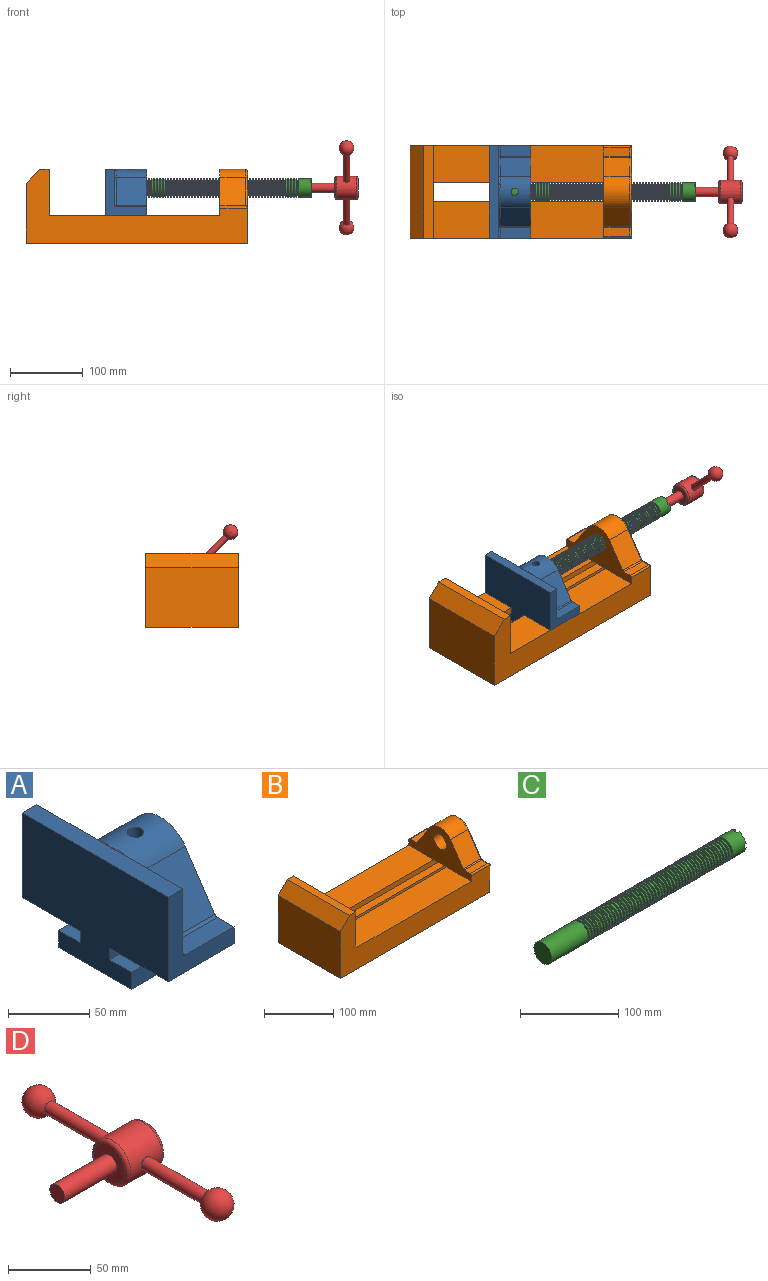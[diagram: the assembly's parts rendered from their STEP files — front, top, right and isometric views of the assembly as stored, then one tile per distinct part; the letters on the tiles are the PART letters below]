
ASSEMBLY  parts=4 mates=3
PART A: 36 faces, bbox 57.2x127x89 mm
  f0: plane 57.15x50.8mm, normal (0,0,-1), area 2903.2mm2, adj f6,f9,f10,f23
  f1: cylinder r=12.7mm len=44.45mm, axis (1,0,0), area 3464.3mm2, adj f6,f15,f16
  f2: plane 41.91x14.52mm, normal (0,0,1), area 608.5mm2, adj f6,f11,f24,f25
  f3: plane 51.86x48.26mm, normal (1,0,0), area 1495.7mm2, adj f8,f10,f31,f33,f35
  f4: plane 51.86x48.26mm, normal (1,0,0), area 1495.7mm2, adj f8,f11,f24,f28,f29
  f5: plane 57.15x50.8mm, normal (0,0,-1), area 2903.2mm2, adj f6,f9,f11,f22
  f6: plane 127x85.09mm, normal (1,0,0), area 5190.6mm2, adj f0,f1,f2,f5,f7,f10,f11,f12
  f7: plane 41.91x14.52mm, normal (0,0,1), area 608.5mm2, adj f6,f10,f30,f31
  f8: plane 127x12.7mm, normal (0,0,1), area 1612.9mm2, adj f3,f4,f9,f10,f11,f26,f34
  f9: plane 127x85.09mm, normal (-1,0,0), area 9096.8mm2, adj f0,f5,f8,f10,f11,f17,f18,f19
  f10: plane 63.5x57.15mm, normal (0,-1,0), area 1372.3mm2, adj f0,f3,f6,f7,f8,f9,f31
  f11: plane 63.5x57.15mm, normal (0,1,0), area 1372.3mm2, adj f2,f4,f5,f6,f8,f9,f24
  f12: plane 41.91x38.43mm, normal (0,-0.83,0.56), area 1939.2mm2, adj f6,f13,f30,f33
  f13: cylinder r=25.4mm len=44.45mm, axis (1,0,0), area 2026.5mm2, adj f6,f12,f14,f16,f26,f28,f34,f35
  f14: plane 41.91x38.43mm, normal (0,0.83,0.56), area 1939.2mm2, adj f6,f13,f25,f29
  f15: plane 25.4x25.4mm, normal (1,0,0), area 506.7mm2, adj f1
  f16: cylinder r=5.08mm len=13.76mm, axis (0,0,1), area 414mm2, adj f1,f13
  f17: plane 57.15x19.05mm, normal (0,0,1), area 1088.7mm2, adj f6,f9,f18,f23
  f18: plane 57.15x12.7mm, normal (0,-1,0), area 725.8mm2, adj f6,f9,f17,f19
  f19: plane 63.5x57.15mm, normal (0,0,-1), area 3629mm2, adj f6,f9,f18,f20
  f20: plane 57.15x12.7mm, normal (0,1,0), area 725.8mm2, adj f6,f9,f19,f21
  f21: plane 57.15x19.05mm, normal (0,0,1), area 1088.7mm2, adj f6,f9,f20,f22
  f22: plane 57.15x8.89mm, normal (0,1,0), area 508.1mm2, adj f5,f6,f9,f21
  f23: plane 57.15x8.89mm, normal (0,-1,0), area 508.1mm2, adj f0,f6,f9,f17
  f24: cylinder r=2.54mm len=14.52mm, axis (0,-1,0), area 57.9mm2, adj f2,f4,f11,f27
  f25: cylinder r=2.54mm len=41.91mm, axis (1,0,0), area 104.3mm2, adj f2,f6,f14,f27
  f26: bspline ~12.24x2.8mm, area 20.9mm2, adj f8,f13,f28
  f27: sphere r=2.54mm, area 6.3mm2, adj f24,f25,f29
  f28: torus R=27.94mm, axis (1,0,0), area 57.8mm2, adj f4,f13,f26,f29
  f29: cylinder r=2.54mm len=39.84mm, axis (0,-0.56,0.83), area 184.6mm2, adj f4,f14,f27,f28
  f30: cylinder r=2.54mm len=41.91mm, axis (1,0,0), area 104.3mm2, adj f6,f7,f12,f32
  f31: cylinder r=2.54mm len=14.52mm, axis (0,-1,0), area 57.9mm2, adj f3,f7,f10,f32
  f32: sphere r=2.54mm, area 6.3mm2, adj f30,f31,f33
  f33: cylinder r=2.54mm len=39.84mm, axis (0,-0.56,-0.83), area 184.6mm2, adj f3,f12,f32,f35
  f34: bspline ~12.24x2.8mm, area 20.9mm2, adj f8,f13,f35
  f35: torus R=27.94mm, axis (1,0,0), area 57.8mm2, adj f3,f13,f33,f34
PART B: 39 faces, bbox 304.8x127x103.7 mm
  f0: plane 234.95x50.8mm, normal (0,0,1), area 11935.5mm2, adj f3,f8,f16,f26
  f1: plane 127x99.06mm, normal (1,0,0), area 7097.5mm2, adj f7,f8,f9,f14,f17,f18,f19,f20
  f2: plane 234.95x50.8mm, normal (0,0,1), area 11935.5mm2, adj f3,f9,f16,f27
  f3: plane 127x101.6mm, normal (1,0,0), area 9516.1mm2, adj f0,f2,f4,f7,f8,f9,f18,f19
  f4: plane 127x12.7mm, normal (0,0,1), area 1612.9mm2, adj f3,f5,f8,f9
  f5: plane 127x19.05mm, normal (-0.71,0,0.71), area 3421.5mm2, adj f4,f6,f8,f9
  f6: plane 127x82.55mm, normal (-1,0,0), area 10483.8mm2, adj f5,f7,f8,f9
  f7: plane 304.8x127mm, normal (0,0,-1), area 31774.1mm2, adj f1,f3,f6,f8,f9,f21,f22
  f8: plane 304.8x101.6mm, normal (0,-1,0), area 13834.6mm2, adj f0,f1,f3,f4,f5,f6,f7,f16
  f9: plane 304.8x101.6mm, normal (0,1,0), area 13834.6mm2, adj f1,f2,f3,f4,f5,f6,f7,f16
  f10: plane 35.56x11.98mm, normal (0,0,1), area 426mm2, adj f16,f28,f29,f30
  f11: plane 38.43x35.56mm, normal (0,0.83,0.56), area 1645.4mm2, adj f12,f16,f29,f32
  f12: cylinder r=25.4mm len=42.19mm, axis (1,0,0), area 1770.2mm2, adj f11,f13,f16,f33
  f13: plane 38.43x35.56mm, normal (0,-0.83,0.56), area 1645.4mm2, adj f12,f16,f34,f35
  f14: cylinder r=12.7mm len=38.1mm, axis (1,0,0), area 3040.2mm2, adj f1,f16
  f15: plane 35.56x11.98mm, normal (0,0,1), area 426mm2, adj f16,f34,f36,f38
  f16: plane 127x63.5mm, normal (-1,0,0), area 4155.5mm2, adj f0,f2,f8,f9,f10,f11,f12,f13
  f17: plane 38.1x25.4mm, normal (0,0,-1), area 967.7mm2, adj f1,f16,f26,f27
  f18: plane 273.05x19.05mm, normal (0,0,-1), area 5201.6mm2, adj f1,f3,f19,f26
  f19: plane 273.05x12.7mm, normal (0,1,0), area 3467.7mm2, adj f1,f3,f18,f20
  f20: plane 273.05x19.05mm, normal (0,0,1), area 5201.6mm2, adj f1,f3,f19,f21
  f21: plane 273.05x16.51mm, normal (0,1,0), area 4508.1mm2, adj f1,f3,f7,f20
  f22: plane 273.05x16.51mm, normal (0,-1,0), area 4508.1mm2, adj f1,f3,f7,f23
  f23: plane 273.05x19.05mm, normal (0,0,1), area 5201.6mm2, adj f1,f3,f22,f24
  f24: plane 273.05x12.7mm, normal (0,-1,0), area 3467.7mm2, adj f1,f3,f23,f25
  f25: plane 273.05x19.05mm, normal (0,0,-1), area 5201.6mm2, adj f1,f3,f24,f27
  f26: plane 273.05x8.89mm, normal (0,1,0), area 2427.4mm2, adj f0,f1,f3,f17,f18
  f27: plane 273.05x8.89mm, normal (0,-1,0), area 2427.4mm2, adj f1,f2,f3,f17,f25
  f28: cylinder r=2.54mm len=38.1mm, axis (1,0,0), area 148.3mm2, adj f9,f10,f16,f30
  f29: cylinder r=2.54mm len=35.56mm, axis (-1,0,0), area 88.5mm2, adj f10,f11,f16,f31
  f30: cylinder r=2.54mm len=14.52mm, axis (0,1,0), area 54.3mm2, adj f1,f10,f28,f31
  f31: torus R=5.08mm, axis (-1,0,0), area 13.5mm2, adj f1,f29,f30,f32
  f32: cylinder r=2.54mm len=39.84mm, axis (0,0.56,-0.83), area 184.6mm2, adj f1,f11,f31,f33
  f33: torus R=22.86mm, axis (-1,0,0), area 191.4mm2, adj f1,f12,f32,f35
  f34: cylinder r=2.54mm len=35.56mm, axis (-1,0,0), area 88.5mm2, adj f13,f15,f16,f37
  f35: cylinder r=2.54mm len=39.84mm, axis (0,0.56,0.83), area 184.6mm2, adj f1,f13,f33,f37
  f36: cylinder r=2.54mm len=38.1mm, axis (-1,0,0), area 148.3mm2, adj f8,f15,f16,f38
  f37: torus R=5.08mm, axis (-1,0,0), area 13.5mm2, adj f1,f34,f35,f38
  f38: cylinder r=2.54mm len=14.52mm, axis (0,1,0), area 54.3mm2, adj f1,f15,f36,f37
PART C: 220 faces, bbox 279.4x25.4x25.4 mm
  f0: cylinder r=12.7mm len=25.4mm, axis (-1,0,0), area 1468.2mm2, adj f1,f2,f3,f5,f7,f208,f209,f210
  f1: plane 9.9x9.9mm, normal (1,0,0), area 62.3mm2, adj f0,f4,f213,f216
  f2: plane 9.9x9.9mm, normal (1,0,0), area 62.3mm2, adj f0,f4,f210,f218
  f3: plane 9.9x9.9mm, normal (1,0,0), area 62.3mm2, adj f0,f4,f209,f212
  f4: cylinder r=6.35mm len=25.4mm, axis (1,0,0), area 960.3mm2, adj f1,f2,f3,f5,f6,f208,f209,f210
  f5: plane 9.9x9.9mm, normal (1,0,0), area 62.3mm2, adj f0,f4,f215,f217
  f6: plane 12.7x12.7mm, normal (1,0,0), area 126.7mm2, adj f4
  f7: cone r=12.7mm half-angle=76deg, axis (1,0,0), area 188mm2, adj f0,f9
  f8: cone r=10.16mm half-angle=76deg, axis (-1,0,0), area 188mm2, adj f9,f10
  f9: cylinder r=10.16mm len=20.32mm, axis (1,0,0), area 81.1mm2, adj f7,f8
  f10: cylinder r=12.7mm len=25.4mm, axis (-1,0,0), area 131.7mm2, adj f8,f11
  f11: cone r=12.7mm half-angle=76deg, axis (1,0,0), area 188mm2, adj f10,f13
  f12: cone r=10.16mm half-angle=76deg, axis (-1,0,0), area 188mm2, adj f13,f14
  f13: cylinder r=10.16mm len=20.32mm, axis (1,0,0), area 81.1mm2, adj f11,f12
  f14: cylinder r=12.7mm len=25.4mm, axis (-1,0,0), area 131.7mm2, adj f12,f15
  f15: cone r=12.7mm half-angle=76deg, axis (1,0,0), area 188mm2, adj f14,f17
  f16: cone r=10.16mm half-angle=76deg, axis (-1,0,0), area 188mm2, adj f17,f18
  f17: cylinder r=10.16mm len=20.32mm, axis (1,0,0), area 81.1mm2, adj f15,f16
  f18: cylinder r=12.7mm len=25.4mm, axis (-1,0,0), area 131.7mm2, adj f16,f19
  f19: cone r=12.7mm half-angle=76deg, axis (1,0,0), area 188mm2, adj f18,f21
  f20: cone r=10.16mm half-angle=76deg, axis (-1,0,0), area 188mm2, adj f21,f22
  f21: cylinder r=10.16mm len=20.32mm, axis (1,0,0), area 81.1mm2, adj f19,f20
  f22: cylinder r=12.7mm len=25.4mm, axis (-1,0,0), area 131.7mm2, adj f20,f23
  f23: cone r=12.7mm half-angle=76deg, axis (1,0,0), area 188mm2, adj f22,f25
  f24: cone r=10.16mm half-angle=76deg, axis (-1,0,0), area 188mm2, adj f25,f26
  f25: cylinder r=10.16mm len=20.32mm, axis (1,0,0), area 81.1mm2, adj f23,f24
  f26: cylinder r=12.7mm len=25.4mm, axis (-1,0,0), area 131.7mm2, adj f24,f27
  f27: cone r=12.7mm half-angle=76deg, axis (1,0,0), area 188mm2, adj f26,f29
  f28: cone r=10.16mm half-angle=76deg, axis (-1,0,0), area 188mm2, adj f29,f30
  f29: cylinder r=10.16mm len=20.32mm, axis (1,0,0), area 81.1mm2, adj f27,f28
  f30: cylinder r=12.7mm len=25.4mm, axis (-1,0,0), area 131.7mm2, adj f28,f31
  f31: cone r=12.7mm half-angle=76deg, axis (1,0,0), area 188mm2, adj f30,f33
  f32: cone r=10.16mm half-angle=76deg, axis (-1,0,0), area 188mm2, adj f33,f34
  f33: cylinder r=10.16mm len=20.32mm, axis (1,0,0), area 81.1mm2, adj f31,f32
  f34: cylinder r=12.7mm len=25.4mm, axis (-1,0,0), area 131.7mm2, adj f32,f35
  f35: cone r=12.7mm half-angle=76deg, axis (1,0,0), area 188mm2, adj f34,f37
  f36: cone r=10.16mm half-angle=76deg, axis (-1,0,0), area 188mm2, adj f37,f38
  f37: cylinder r=10.16mm len=20.32mm, axis (1,0,0), area 81.1mm2, adj f35,f36
  f38: cylinder r=12.7mm len=25.4mm, axis (-1,0,0), area 131.7mm2, adj f36,f39
  f39: cone r=12.7mm half-angle=76deg, axis (1,0,0), area 188mm2, adj f38,f41
  f40: cone r=10.16mm half-angle=76deg, axis (-1,0,0), area 188mm2, adj f41,f42
  f41: cylinder r=10.16mm len=20.32mm, axis (1,0,0), area 81.1mm2, adj f39,f40
  f42: cylinder r=12.7mm len=25.4mm, axis (-1,0,0), area 131.7mm2, adj f40,f43
  f43: cone r=12.7mm half-angle=76deg, axis (1,0,0), area 188mm2, adj f42,f45
  f44: cone r=10.16mm half-angle=76deg, axis (-1,0,0), area 188mm2, adj f45,f46
  f45: cylinder r=10.16mm len=20.32mm, axis (1,0,0), area 81.1mm2, adj f43,f44
  f46: cylinder r=12.7mm len=25.4mm, axis (-1,0,0), area 131.7mm2, adj f44,f47
  f47: cone r=12.7mm half-angle=76deg, axis (1,0,0), area 188mm2, adj f46,f49
  f48: cone r=10.16mm half-angle=76deg, axis (-1,0,0), area 188mm2, adj f49,f50
  f49: cylinder r=10.16mm len=20.32mm, axis (1,0,0), area 81.1mm2, adj f47,f48
  f50: cylinder r=12.7mm len=25.4mm, axis (-1,0,0), area 131.7mm2, adj f48,f51
  f51: cone r=12.7mm half-angle=76deg, axis (1,0,0), area 188mm2, adj f50,f53
  f52: cone r=10.16mm half-angle=76deg, axis (-1,0,0), area 188mm2, adj f53,f54
  f53: cylinder r=10.16mm len=20.32mm, axis (1,0,0), area 81.1mm2, adj f51,f52
  f54: cylinder r=12.7mm len=25.4mm, axis (-1,0,0), area 131.7mm2, adj f52,f55
  f55: cone r=12.7mm half-angle=76deg, axis (1,0,0), area 188mm2, adj f54,f57
  f56: cone r=10.16mm half-angle=76deg, axis (-1,0,0), area 188mm2, adj f57,f58
  f57: cylinder r=10.16mm len=20.32mm, axis (1,0,0), area 81.1mm2, adj f55,f56
  f58: cylinder r=12.7mm len=25.4mm, axis (-1,0,0), area 131.7mm2, adj f56,f59
  f59: cone r=12.7mm half-angle=76deg, axis (1,0,0), area 188mm2, adj f58,f61
  f60: cone r=10.16mm half-angle=76deg, axis (-1,0,0), area 188mm2, adj f61,f62
  f61: cylinder r=10.16mm len=20.32mm, axis (1,0,0), area 81.1mm2, adj f59,f60
  f62: cylinder r=12.7mm len=25.4mm, axis (-1,0,0), area 131.7mm2, adj f60,f63
  f63: cone r=12.7mm half-angle=76deg, axis (1,0,0), area 188mm2, adj f62,f65
  f64: cone r=10.16mm half-angle=76deg, axis (-1,0,0), area 188mm2, adj f65,f66
  f65: cylinder r=10.16mm len=20.32mm, axis (1,0,0), area 81.1mm2, adj f63,f64
  f66: cylinder r=12.7mm len=25.4mm, axis (-1,0,0), area 131.7mm2, adj f64,f67
  f67: cone r=12.7mm half-angle=76deg, axis (1,0,0), area 188mm2, adj f66,f69
  f68: cone r=10.16mm half-angle=76deg, axis (-1,0,0), area 188mm2, adj f69,f70
  f69: cylinder r=10.16mm len=20.32mm, axis (1,0,0), area 81.1mm2, adj f67,f68
  f70: cylinder r=12.7mm len=25.4mm, axis (-1,0,0), area 131.7mm2, adj f68,f71
  f71: cone r=12.7mm half-angle=76deg, axis (1,0,0), area 188mm2, adj f70,f73
  f72: cone r=10.16mm half-angle=76deg, axis (-1,0,0), area 188mm2, adj f73,f74
  f73: cylinder r=10.16mm len=20.32mm, axis (1,0,0), area 81.1mm2, adj f71,f72
  f74: cylinder r=12.7mm len=25.4mm, axis (-1,0,0), area 131.7mm2, adj f72,f75
  f75: cone r=12.7mm half-angle=76deg, axis (1,0,0), area 188mm2, adj f74,f77
  f76: cone r=10.16mm half-angle=76deg, axis (-1,0,0), area 188mm2, adj f77,f78
  f77: cylinder r=10.16mm len=20.32mm, axis (1,0,0), area 81.1mm2, adj f75,f76
  f78: cylinder r=12.7mm len=25.4mm, axis (-1,0,0), area 131.7mm2, adj f76,f79
  f79: cone r=12.7mm half-angle=76deg, axis (1,0,0), area 188mm2, adj f78,f81
  f80: cone r=10.16mm half-angle=76deg, axis (-1,0,0), area 188mm2, adj f81,f82
  f81: cylinder r=10.16mm len=20.32mm, axis (1,0,0), area 81.1mm2, adj f79,f80
  f82: cylinder r=12.7mm len=25.4mm, axis (-1,0,0), area 131.7mm2, adj f80,f83
  f83: cone r=12.7mm half-angle=76deg, axis (1,0,0), area 188mm2, adj f82,f85
  f84: cone r=10.16mm half-angle=76deg, axis (-1,0,0), area 188mm2, adj f85,f86
  f85: cylinder r=10.16mm len=20.32mm, axis (1,0,0), area 81.1mm2, adj f83,f84
  f86: cylinder r=12.7mm len=25.4mm, axis (-1,0,0), area 131.7mm2, adj f84,f87
  f87: cone r=12.7mm half-angle=76deg, axis (1,0,0), area 188mm2, adj f86,f89
  f88: cone r=10.16mm half-angle=76deg, axis (-1,0,0), area 188mm2, adj f89,f90
  f89: cylinder r=10.16mm len=20.32mm, axis (1,0,0), area 81.1mm2, adj f87,f88
  f90: cylinder r=12.7mm len=25.4mm, axis (-1,0,0), area 131.7mm2, adj f88,f91
  f91: cone r=12.7mm half-angle=76deg, axis (1,0,0), area 188mm2, adj f90,f93
  f92: cone r=10.16mm half-angle=76deg, axis (-1,0,0), area 188mm2, adj f93,f94
  f93: cylinder r=10.16mm len=20.32mm, axis (1,0,0), area 81.1mm2, adj f91,f92
  f94: cylinder r=12.7mm len=25.4mm, axis (-1,0,0), area 131.7mm2, adj f92,f95
  f95: cone r=12.7mm half-angle=76deg, axis (1,0,0), area 188mm2, adj f94,f97
  f96: cone r=10.16mm half-angle=76deg, axis (-1,0,0), area 188mm2, adj f97,f98
  f97: cylinder r=10.16mm len=20.32mm, axis (1,0,0), area 81.1mm2, adj f95,f96
  f98: cylinder r=12.7mm len=25.4mm, axis (-1,0,0), area 131.7mm2, adj f96,f99
  f99: cone r=12.7mm half-angle=76deg, axis (1,0,0), area 188mm2, adj f98,f101
  f100: cone r=10.16mm half-angle=76deg, axis (-1,0,0), area 188mm2, adj f101,f102
  f101: cylinder r=10.16mm len=20.32mm, axis (1,0,0), area 81.1mm2, adj f99,f100
  f102: cylinder r=12.7mm len=25.4mm, axis (-1,0,0), area 131.7mm2, adj f100,f103
  f103: cone r=12.7mm half-angle=76deg, axis (1,0,0), area 188mm2, adj f102,f105
  f104: cone r=10.16mm half-angle=76deg, axis (-1,0,0), area 188mm2, adj f105,f106
  f105: cylinder r=10.16mm len=20.32mm, axis (1,0,0), area 81.1mm2, adj f103,f104
  f106: cylinder r=12.7mm len=25.4mm, axis (-1,0,0), area 131.7mm2, adj f104,f107
  f107: cone r=12.7mm half-angle=76deg, axis (1,0,0), area 188mm2, adj f106,f109
  f108: cone r=10.16mm half-angle=76deg, axis (-1,0,0), area 188mm2, adj f109,f110
  f109: cylinder r=10.16mm len=20.32mm, axis (1,0,0), area 81.1mm2, adj f107,f108
  f110: cylinder r=12.7mm len=25.4mm, axis (-1,0,0), area 131.7mm2, adj f108,f111
  f111: cone r=12.7mm half-angle=76deg, axis (1,0,0), area 188mm2, adj f110,f113
  f112: cone r=10.16mm half-angle=76deg, axis (-1,0,0), area 188mm2, adj f113,f114
  f113: cylinder r=10.16mm len=20.32mm, axis (1,0,0), area 81.1mm2, adj f111,f112
  f114: cylinder r=12.7mm len=25.4mm, axis (-1,0,0), area 131.7mm2, adj f112,f115
  f115: cone r=12.7mm half-angle=76deg, axis (1,0,0), area 188mm2, adj f114,f117
  f116: cone r=10.16mm half-angle=76deg, axis (-1,0,0), area 188mm2, adj f117,f118
  f117: cylinder r=10.16mm len=20.32mm, axis (1,0,0), area 81.1mm2, adj f115,f116
  f118: cylinder r=12.7mm len=25.4mm, axis (-1,0,0), area 131.7mm2, adj f116,f119
  f119: cone r=12.7mm half-angle=76deg, axis (1,0,0), area 188mm2, adj f118,f121
  f120: cone r=10.16mm half-angle=76deg, axis (-1,0,0), area 188mm2, adj f121,f122
  f121: cylinder r=10.16mm len=20.32mm, axis (1,0,0), area 81.1mm2, adj f119,f120
  f122: cylinder r=12.7mm len=25.4mm, axis (-1,0,0), area 131.7mm2, adj f120,f123
  f123: cone r=12.7mm half-angle=76deg, axis (1,0,0), area 188mm2, adj f122,f125
  f124: cone r=10.16mm half-angle=76deg, axis (-1,0,0), area 188mm2, adj f125,f126
  f125: cylinder r=10.16mm len=20.32mm, axis (1,0,0), area 81.1mm2, adj f123,f124
  f126: cylinder r=12.7mm len=25.4mm, axis (-1,0,0), area 131.7mm2, adj f124,f127
  f127: cone r=12.7mm half-angle=76deg, axis (1,0,0), area 188mm2, adj f126,f129
  f128: cone r=10.16mm half-angle=76deg, axis (-1,0,0), area 188mm2, adj f129,f130
  f129: cylinder r=10.16mm len=20.32mm, axis (1,0,0), area 81.1mm2, adj f127,f128
  f130: cylinder r=12.7mm len=25.4mm, axis (-1,0,0), area 131.7mm2, adj f128,f131
  f131: cone r=12.7mm half-angle=76deg, axis (1,0,0), area 188mm2, adj f130,f133
  f132: cone r=10.16mm half-angle=76deg, axis (-1,0,0), area 188mm2, adj f133,f134
  f133: cylinder r=10.16mm len=20.32mm, axis (1,0,0), area 81.1mm2, adj f131,f132
  f134: cylinder r=12.7mm len=25.4mm, axis (-1,0,0), area 131.7mm2, adj f132,f135
  f135: cone r=12.7mm half-angle=76deg, axis (1,0,0), area 188mm2, adj f134,f137
  f136: cone r=10.16mm half-angle=76deg, axis (-1,0,0), area 188mm2, adj f137,f138
  f137: cylinder r=10.16mm len=20.32mm, axis (1,0,0), area 81.1mm2, adj f135,f136
  f138: cylinder r=12.7mm len=25.4mm, axis (-1,0,0), area 131.7mm2, adj f136,f139
  f139: cone r=12.7mm half-angle=76deg, axis (1,0,0), area 188mm2, adj f138,f141
  f140: cone r=10.16mm half-angle=76deg, axis (-1,0,0), area 188mm2, adj f141,f142
  f141: cylinder r=10.16mm len=20.32mm, axis (1,0,0), area 81.1mm2, adj f139,f140
  f142: cylinder r=12.7mm len=25.4mm, axis (-1,0,0), area 131.7mm2, adj f140,f143
  f143: cone r=12.7mm half-angle=76deg, axis (1,0,0), area 188mm2, adj f142,f145
  f144: cone r=10.16mm half-angle=76deg, axis (-1,0,0), area 188mm2, adj f145,f146
  f145: cylinder r=10.16mm len=20.32mm, axis (1,0,0), area 81.1mm2, adj f143,f144
  f146: cylinder r=12.7mm len=25.4mm, axis (-1,0,0), area 131.7mm2, adj f144,f147
  f147: cone r=12.7mm half-angle=76deg, axis (1,0,0), area 188mm2, adj f146,f149
  f148: cone r=10.16mm half-angle=76deg, axis (-1,0,0), area 188mm2, adj f149,f150
  f149: cylinder r=10.16mm len=20.32mm, axis (1,0,0), area 81.1mm2, adj f147,f148
  f150: cylinder r=12.7mm len=25.4mm, axis (-1,0,0), area 131.7mm2, adj f148,f151
  f151: cone r=12.7mm half-angle=76deg, axis (1,0,0), area 188mm2, adj f150,f153
  f152: cone r=10.16mm half-angle=76deg, axis (-1,0,0), area 188mm2, adj f153,f154
  f153: cylinder r=10.16mm len=20.32mm, axis (1,0,0), area 81.1mm2, adj f151,f152
  f154: cylinder r=12.7mm len=25.4mm, axis (-1,0,0), area 131.7mm2, adj f152,f155
  f155: cone r=12.7mm half-angle=76deg, axis (1,0,0), area 188mm2, adj f154,f157
  f156: cone r=10.16mm half-angle=76deg, axis (-1,0,0), area 188mm2, adj f157,f158
  f157: cylinder r=10.16mm len=20.32mm, axis (1,0,0), area 81.1mm2, adj f155,f156
  f158: cylinder r=12.7mm len=25.4mm, axis (-1,0,0), area 131.7mm2, adj f156,f159
  f159: cone r=12.7mm half-angle=76deg, axis (1,0,0), area 188mm2, adj f158,f161
  f160: cone r=10.16mm half-angle=76deg, axis (-1,0,0), area 188mm2, adj f161,f162
  f161: cylinder r=10.16mm len=20.32mm, axis (1,0,0), area 81.1mm2, adj f159,f160
  f162: cylinder r=12.7mm len=25.4mm, axis (-1,0,0), area 131.7mm2, adj f160,f163
  f163: cone r=12.7mm half-angle=76deg, axis (1,0,0), area 188mm2, adj f162,f165
  f164: cone r=10.16mm half-angle=76deg, axis (-1,0,0), area 188mm2, adj f165,f166
  f165: cylinder r=10.16mm len=20.32mm, axis (1,0,0), area 81.1mm2, adj f163,f164
  f166: cylinder r=12.7mm len=25.4mm, axis (-1,0,0), area 131.7mm2, adj f164,f167
  f167: cone r=12.7mm half-angle=76deg, axis (1,0,0), area 188mm2, adj f166,f169
  f168: cone r=10.16mm half-angle=76deg, axis (-1,0,0), area 188mm2, adj f169,f170
  f169: cylinder r=10.16mm len=20.32mm, axis (1,0,0), area 81.1mm2, adj f167,f168
  f170: cylinder r=12.7mm len=25.4mm, axis (-1,0,0), area 131.7mm2, adj f168,f171
  f171: cone r=12.7mm half-angle=76deg, axis (1,0,0), area 188mm2, adj f170,f173
  f172: cone r=10.16mm half-angle=76deg, axis (-1,0,0), area 188mm2, adj f173,f174
  f173: cylinder r=10.16mm len=20.32mm, axis (1,0,0), area 81.1mm2, adj f171,f172
  f174: cylinder r=12.7mm len=25.4mm, axis (-1,0,0), area 131.7mm2, adj f172,f175
  f175: cone r=12.7mm half-angle=76deg, axis (1,0,0), area 188mm2, adj f174,f177
  f176: cone r=10.16mm half-angle=76deg, axis (-1,0,0), area 188mm2, adj f177,f178
  f177: cylinder r=10.16mm len=20.32mm, axis (1,0,0), area 81.1mm2, adj f175,f176
  f178: cylinder r=12.7mm len=25.4mm, axis (-1,0,0), area 131.7mm2, adj f176,f179
  f179: cone r=12.7mm half-angle=76deg, axis (1,0,0), area 188mm2, adj f178,f181
  f180: cone r=10.16mm half-angle=76deg, axis (-1,0,0), area 188mm2, adj f181,f182
  f181: cylinder r=10.16mm len=20.32mm, axis (1,0,0), area 81.1mm2, adj f179,f180
  f182: cylinder r=12.7mm len=25.4mm, axis (-1,0,0), area 131.7mm2, adj f180,f183
  f183: cone r=12.7mm half-angle=76deg, axis (1,0,0), area 188mm2, adj f182,f185
  f184: cone r=10.16mm half-angle=76deg, axis (-1,0,0), area 188mm2, adj f185,f186
  f185: cylinder r=10.16mm len=20.32mm, axis (1,0,0), area 81.1mm2, adj f183,f184
  f186: cylinder r=12.7mm len=25.4mm, axis (-1,0,0), area 131.7mm2, adj f184,f187
  f187: cone r=12.7mm half-angle=76deg, axis (1,0,0), area 188mm2, adj f186,f189
  f188: cone r=10.16mm half-angle=76deg, axis (-1,0,0), area 188mm2, adj f189,f190
  f189: cylinder r=10.16mm len=20.32mm, axis (1,0,0), area 81.1mm2, adj f187,f188
  f190: cylinder r=12.7mm len=25.4mm, axis (-1,0,0), area 131.7mm2, adj f188,f191
  f191: cone r=12.7mm half-angle=76deg, axis (1,0,0), area 188mm2, adj f190,f193
  f192: cone r=10.16mm half-angle=76deg, axis (-1,0,0), area 188mm2, adj f193,f194
  f193: cylinder r=10.16mm len=20.32mm, axis (1,0,0), area 81.1mm2, adj f191,f192
  f194: cylinder r=12.7mm len=25.4mm, axis (-1,0,0), area 131.7mm2, adj f192,f195
  f195: cone r=12.7mm half-angle=76deg, axis (1,0,0), area 188mm2, adj f194,f197
  f196: cone r=10.16mm half-angle=76deg, axis (-1,0,0), area 188mm2, adj f197,f198
  f197: cylinder r=10.16mm len=20.32mm, axis (1,0,0), area 81.1mm2, adj f195,f196
  f198: cylinder r=12.7mm len=25.4mm, axis (-1,0,0), area 131.7mm2, adj f196,f199
  f199: cone r=12.7mm half-angle=76deg, axis (1,0,0), area 188mm2, adj f198,f201
  f200: cone r=10.16mm half-angle=76deg, axis (-1,0,0), area 188mm2, adj f201,f202
  f201: cylinder r=10.16mm len=20.32mm, axis (1,0,0), area 81.1mm2, adj f199,f200
  f202: cylinder r=12.7mm len=25.4mm, axis (-1,0,0), area 131.7mm2, adj f200,f203
  f203: cone r=12.7mm half-angle=76deg, axis (1,0,0), area 188mm2, adj f202,f205
  f204: cone r=10.16mm half-angle=76deg, axis (-1,0,0), area 188mm2, adj f205,f207
  f205: cylinder r=10.16mm len=20.32mm, axis (1,0,0), area 81.1mm2, adj f203,f204
  f206: plane 25.4x25.4mm, normal (-1,0,0), area 506.7mm2, adj f207
  f207: cylinder r=12.7mm len=52.45mm, axis (-1,0,0), area 4185.4mm2, adj f204,f206
  f208: plane 6.88x5.08mm, normal (1,0,0), area 32.7mm2, adj f0,f4,f209,f210
  f209: plane 6.62x2.54mm, normal (0,-1,0), area 16.8mm2, adj f0,f3,f4,f208
  f210: plane 6.62x2.54mm, normal (0,1,0), area 16.8mm2, adj f0,f2,f4,f208
  f211: plane 6.88x5.08mm, normal (1,0,0), area 32.7mm2, adj f0,f4,f212,f213
  f212: plane 6.62x2.54mm, normal (0,0,1), area 16.8mm2, adj f0,f3,f4,f211
  f213: plane 6.62x2.54mm, normal (0,0,-1), area 16.8mm2, adj f0,f1,f4,f211
  f214: plane 6.88x5.08mm, normal (1,0,0), area 32.7mm2, adj f0,f4,f215,f216
  f215: plane 6.62x2.54mm, normal (0,1,0), area 16.8mm2, adj f0,f4,f5,f214
  f216: plane 6.62x2.54mm, normal (0,-1,0), area 16.8mm2, adj f0,f1,f4,f214
  f217: plane 6.62x2.54mm, normal (0,0,-1), area 16.8mm2, adj f0,f4,f5,f219
  f218: plane 6.62x2.54mm, normal (0,0,1), area 16.8mm2, adj f0,f2,f4,f219
  f219: plane 6.88x5.08mm, normal (1,0,0), area 32.7mm2, adj f0,f4,f217,f218
PART D: 11 faces, bbox 76.2x172.7x34.4 mm
  f0: sphere r=10.16mm, area 1231.8mm2, adj f1
  f1: cylinder r=4.45mm len=51.82mm, axis (0,1,0), area 1438.5mm2, adj f0,f4
  f2: sphere r=10.16mm, area 1231.8mm2, adj f3
  f3: cylinder r=4.45mm len=51.82mm, axis (0,1,0), area 1438.5mm2, adj f2,f4
  f4: cylinder r=15.88mm len=31.75mm, axis (-1,0,0), area 2534.7mm2, adj f1,f3,f9,f10
  f5: cylinder r=6.35mm len=44.45mm, axis (-1,0,0), area 1773.5mm2, adj f6,f8
  f6: plane 12.7x12.7mm, normal (-1,0,0), area 126.7mm2, adj f5
  f7: plane 26.67x26.67mm, normal (1,0,0), area 558.6mm2, adj f10
  f8: plane 26.67x26.67mm, normal (-1,0,0), area 432mm2, adj f5,f9
  f9: torus R=13.33mm, axis (1,0,0), area 374.8mm2, adj f4,f8
  f10: torus R=13.33mm, axis (1,0,0), area 374.8mm2, adj f4,f7
PLACE A t=(50.01,-91.23,-31.87)mm
PLACE B t=(-27.48,-91.23,-31.87)mm fixed
PLACE C rot(axis=(1,0,0),134.2deg) t=(42.01,-36.61,97.46)mm
PLACE D rot(axis=(1,0,0),134.2deg) t=(54.71,-36.61,97.46)mm
MATE slider A.f9 <-> B.f3  axis (-1,0,0) through (-223.04,-154.73,6.23)mm
MATE revolute C.f7 <-> A.f28  axis (1,0,0) through (-165.89,-91.23,44.33)mm
MATE fastened C.f4 <-> D.f5  axis (1,0,0) through (48.36,-91.23,44.33)mm
